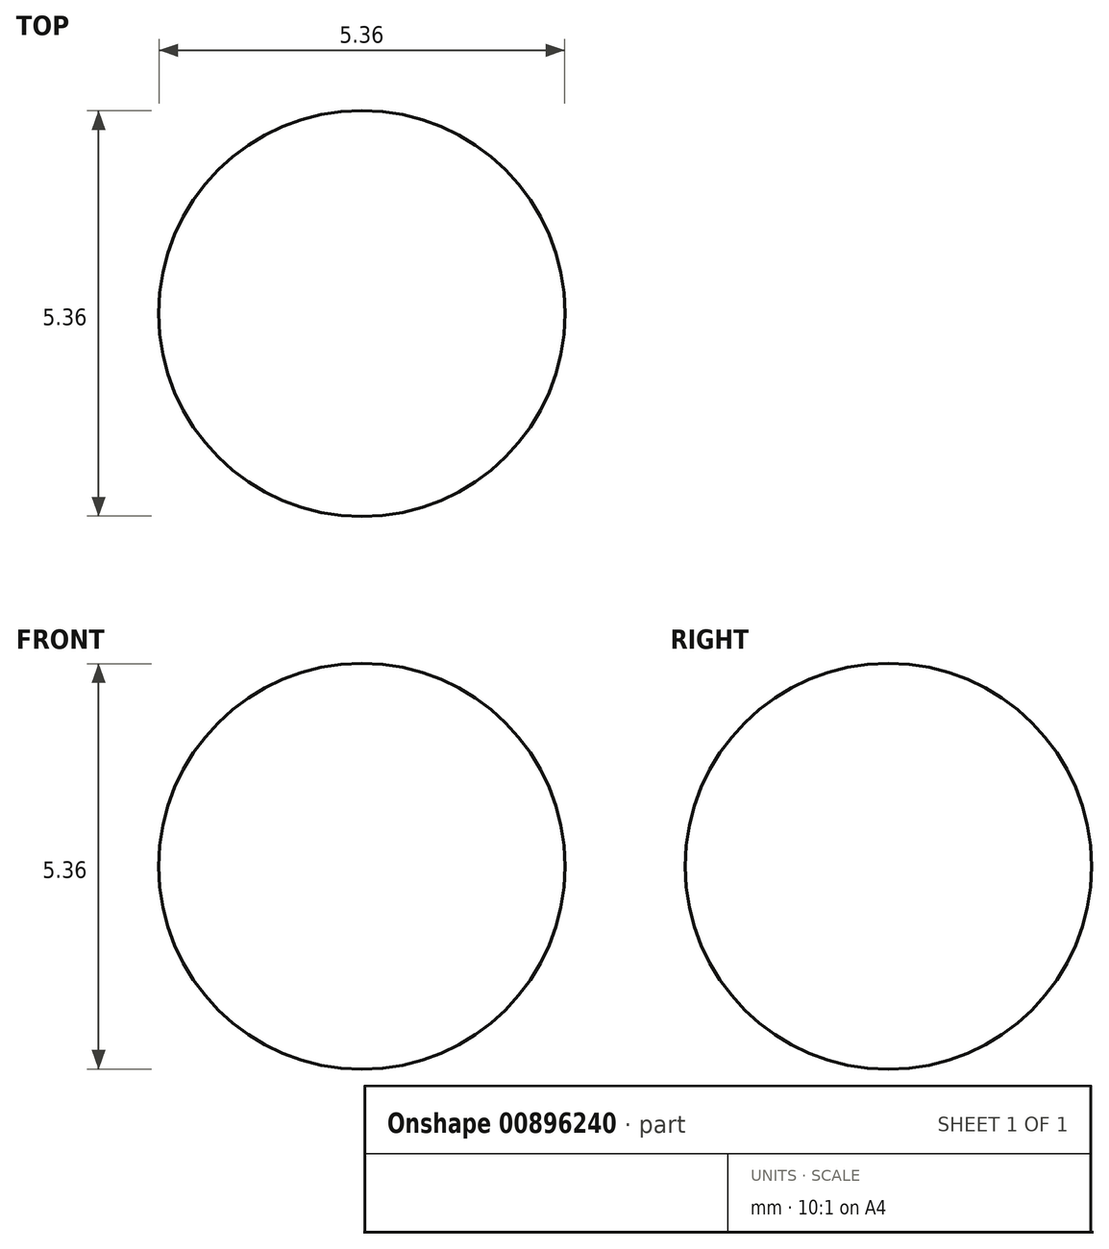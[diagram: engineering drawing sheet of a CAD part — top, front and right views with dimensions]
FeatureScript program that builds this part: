
annotation { "Feature Type Name" : "Feature", "Feature Type Description" : "" }
export const myFeature = defineFeature(function(context is Context, id is Id, definition is map)
    precondition{}
    {
        {
            var Q0;
            Q0=qCreatedBy(makeId("Front.planeOp"),FACE);
            var sketch = newSketch(context, id + "F0", { "sketchPlane" : qUnion([Q0])});
            skArc(sketch, "E0", {"start": v(2.68, 0) * mm, "mid": v(0, 2.68) * mm, "end": v(-2.68, 0) * mm});
            skLineSegment(sketch, "E1", {"start": v(-2.68, 0) * mm, "end": v(2.68, 0) * mm});
            skSolve(sketch);
        }
        {
            var Q0;
            Q0=makeQuery(id+"F0.imprint","IMPRINT",FACE,{"disambiguationData":[TD([[makeQuery(id+"F0.imprint","IMPRINT",EDGE,{"derivedFrom":sQuery(id+"F0.wireOp",EDGE,"E0")}),1.0]])]});
            var Q1;
            Q1=sQuery(id+"F0.wireOp",EDGE,"E1");
            revolve(context, id + "F1", {"surfaceOperationType" : NewSurfaceOperationType.NEW, "entities" : qUnion([Q0]), "axis" : qUnion([Q1]), "revolveType" : RevolveType.FULL});
        }
    });
